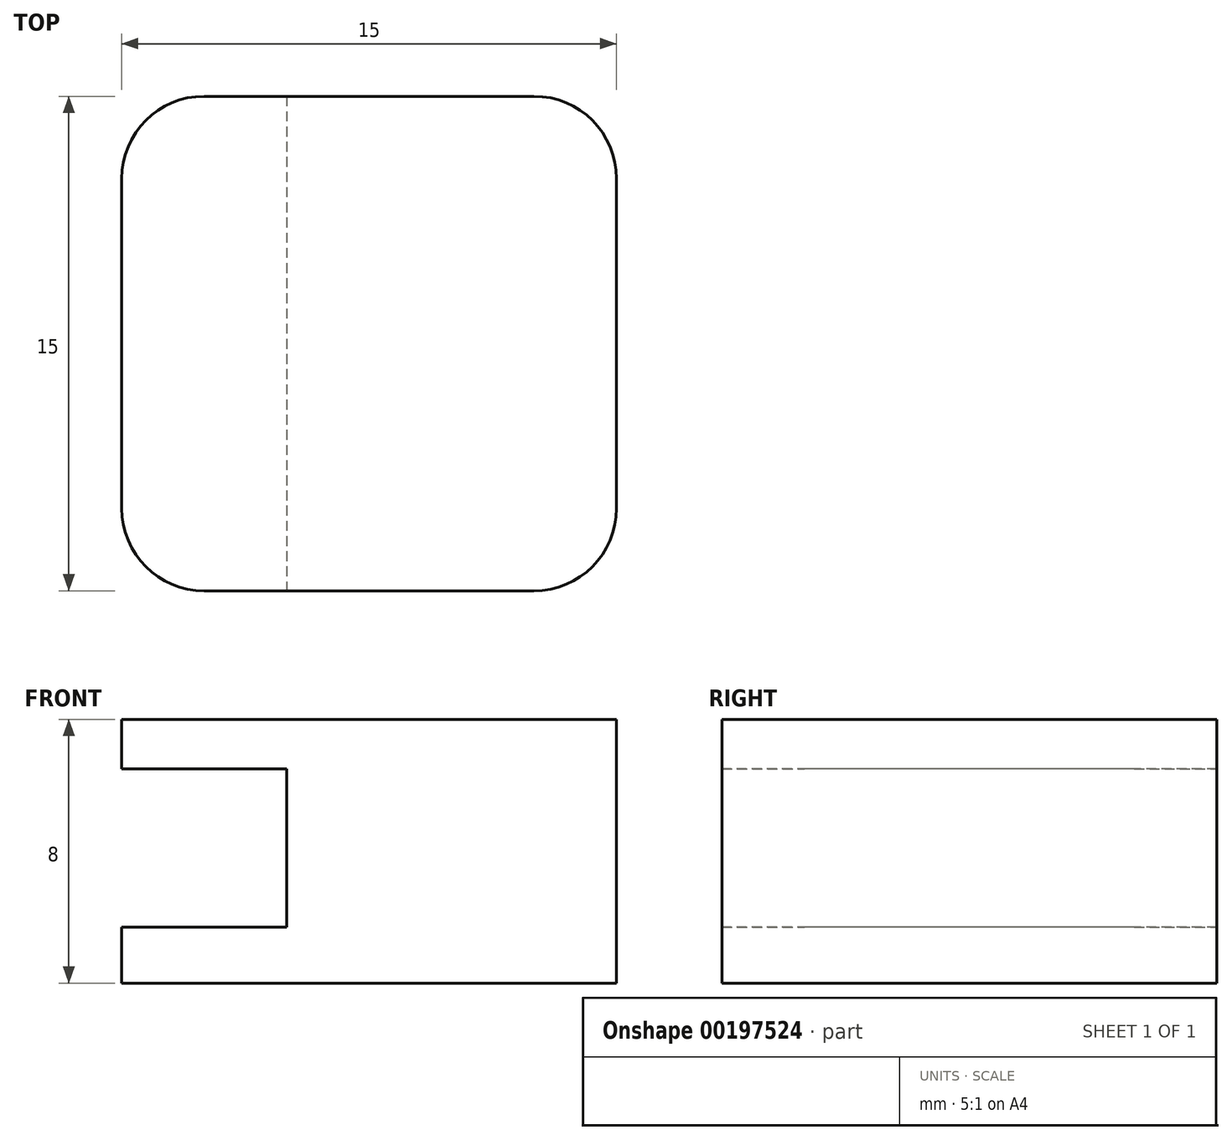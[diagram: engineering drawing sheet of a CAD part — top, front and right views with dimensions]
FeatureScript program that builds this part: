
annotation { "Feature Type Name" : "Feature", "Feature Type Description" : "" }
export const myFeature = defineFeature(function(context is Context, id is Id, definition is map)
    precondition{}
    {
        {
            var Q0;
            Q0=qCreatedBy(makeId("Top.planeOp"),FACE);
            var sketch = newSketch(context, id + "F0", { "sketchPlane" : qUnion([Q0])});
            skLineSegment(sketch, "E0.bottom", {"start": v(-15, 7.5) * mm, "end": v(0, 7.5) * mm});
            skLineSegment(sketch, "E0.top", {"start": v(-15, -7.5) * mm, "end": v(0, -7.5) * mm});
            skLineSegment(sketch, "E0.left", {"start": v(-15, 7.5) * mm, "end": v(-15, -7.5) * mm});
            skLineSegment(sketch, "E0.right", {"start": v(0, 7.5) * mm, "end": v(0, -7.5) * mm});
            skSolve(sketch);
        }
        {
            var Q0;
            Q0=qSketchRegion(id+"F0",true);
            extrude(context, id + "F1", {"entities" : qUnion([Q0]), "depth" : 8 * mm});
        }
        {
            var Q0;
            Q0=makeQuery(id+"F1.opExtrude","SWEPT_FACE",FACE,{"disambiguationData":[OSD([sQuery(id+"F0.wireOp",EDGE,"E0.left")])]});
            var sketch = newSketch(context, id + "F2", { "sketchPlane" : qUnion([Q0])});
            skLineSegment(sketch, "E1.bottom", {"start": v(-7.5, 6.5) * mm, "end": v(7.5, 6.5) * mm});
            skLineSegment(sketch, "E1.top", {"start": v(-7.5, 1.7) * mm, "end": v(7.5, 1.7) * mm});
            skLineSegment(sketch, "E1.left", {"start": v(-7.5, 6.5) * mm, "end": v(-7.5, 1.7) * mm});
            skLineSegment(sketch, "E1.right", {"start": v(7.5, 6.5) * mm, "end": v(7.5, 1.7) * mm});
            skSolve(sketch);
        }
        {
            var Q0;
            Q0=qSketchRegion(id+"F2",true);
            extrude(context, id + "F3", {"entities" : qUnion([Q0]), "operationType" : NewBodyOperationType.REMOVE, "oppositeDirection" : true, "depth" : 5 * mm});
        }
        {
            var Q0;
            Q0=makeQuery(id+"F1.opExtrude","SWEPT_EDGE",EDGE,{"disambiguationData":[OSD([sQuery(id+"F0.wireOp",EDGE,"E0.top"),sQuery(id+"F0.wireOp",EDGE,"E0.right")])]});
            var Q1;
            Q1=makeQuery(id+"F1.opExtrude","SWEPT_EDGE",EDGE,{"disambiguationData":[OSD([sQuery(id+"F0.wireOp",EDGE,"E0.bottom"),sQuery(id+"F0.wireOp",EDGE,"E0.right")])]});
            fillet(context, id + "F4", {"entities" : qUnion([Q0, Q1]), "radius" : 2.5 * mm, "tangentPropagation" : true, "allowEdgeOverflow" : false});
        }
        {
            var Q0;
            {var subQ0=sQuery(id+"F0.wireOp",EDGE,"E0.left");var subQ1=sQuery(id+"F0.wireOp",EDGE,"E0.top");Q0=makeQuery(id+"F3.boolean.opBoolean","SPLIT",EDGE,{"disambiguationData":[TD([makeQuery(id+"F3.opExtrude","SWEPT_FACE",FACE,{"disambiguationData":[OSD([sQuery(id+"F2.wireOp",EDGE,"E1.bottom")])]})])],"derivedFrom":makeQuery(id+"F1.opExtrude","SWEPT_EDGE",EDGE,{"disambiguationData":[OSD([subQ1,subQ0])]})});}
            var Q1;
            {var subQ0=sQuery(id+"F0.wireOp",EDGE,"E0.bottom");var subQ1=sQuery(id+"F0.wireOp",EDGE,"E0.left");Q1=makeQuery(id+"F3.boolean.opBoolean","SPLIT",EDGE,{"disambiguationData":[TD([makeQuery(id+"F3.opExtrude","SWEPT_FACE",FACE,{"disambiguationData":[OSD([sQuery(id+"F2.wireOp",EDGE,"E1.bottom")])]})])],"derivedFrom":makeQuery(id+"F1.opExtrude","SWEPT_EDGE",EDGE,{"disambiguationData":[OSD([subQ0,subQ1])]})});}
            var Q2;
            {var subQ0=sQuery(id+"F0.wireOp",EDGE,"E0.left");var subQ1=sQuery(id+"F0.wireOp",EDGE,"E0.top");Q2=makeQuery(id+"F3.boolean.opBoolean","SPLIT",EDGE,{"disambiguationData":[TD([makeQuery(id+"F3.opExtrude","SWEPT_FACE",FACE,{"disambiguationData":[OSD([sQuery(id+"F2.wireOp",EDGE,"E1.top")])]})])],"derivedFrom":makeQuery(id+"F1.opExtrude","SWEPT_EDGE",EDGE,{"disambiguationData":[OSD([subQ1,subQ0])]})});}
            var Q3;
            {var subQ0=sQuery(id+"F0.wireOp",EDGE,"E0.bottom");var subQ1=sQuery(id+"F0.wireOp",EDGE,"E0.left");Q3=makeQuery(id+"F3.boolean.opBoolean","SPLIT",EDGE,{"disambiguationData":[TD([makeQuery(id+"F3.opExtrude","SWEPT_FACE",FACE,{"disambiguationData":[OSD([sQuery(id+"F2.wireOp",EDGE,"E1.top")])]})])],"derivedFrom":makeQuery(id+"F1.opExtrude","SWEPT_EDGE",EDGE,{"disambiguationData":[OSD([subQ0,subQ1])]})});}
            fillet(context, id + "F5", {"entities" : qUnion([Q0, Q1, Q2, Q3]), "radius" : 2.5 * mm, "tangentPropagation" : true, "allowEdgeOverflow" : false});
        }
    });
